# Revit family: НЕВАТОМ_Вентилятор ВР 86-77, Версия 2.с табл
name_source: partatom
category: Оборудование
revit_build: Autodesk Revit 2017 (Build: 20170118_1100(x64)
units: mm (PartAtom-declared; Revit-internal decimal feet)

## family parameters
Всегда вертикально = Да
На основе рабочей плоскости = Нет
Общий = Да
При загрузке вырезать с полостями = Нет
Размер круглого соединителя = Использовать диаметр
Тип детали = Нормальный
Точка расчета площади = Нет

## types (8) — shared parameters
(1.05Dн) = Нет
1.05Dн = Нет
ADSK_Количество = 1
ADSK_Количество фаз = 3
ADSK_Количество фаз числовое = 3
ADSK_Напряжение = 380 В
ADSK_Номинальная мощность = 0 Вт
ADSK_Ток = 0 А
l патрубка = 80 мм
Ключевая пометка = Вентиляция
ТП = НЕВАТОМ_Вентилятор ВР 86-77

## per-type parameters (varying)
- №2.5: (0.9Dн)=Да; (Dн)=Нет; 0.9Dн=Да; A1=162 мм; AA=175 мм; ADSK_Классификация нагрузок=ОВК; BB=175 мм; D=250 мм; D внешний=300 мм; D входного патрубка=250 мм; D/2=50 мм; D1=255 мм; Dн=Нет; H опоры=270 мм; H1=320 мм; L двиг=50 мм; L длина опоры=410 мм; R1=205 мм; R2=160 мм; Type=38 мм; a2=250 мм; b=20 мм; c1=205 мм; c2=205 мм; d двиг=100 мм; h=120 мм; h1=180 мм; h2=155 мм; h3=0 мм; k=30 мм; l двиг=120 мм; l длина=205 мм; r=50 мм; ВР=2.5 мм; Выбор исполнения=0 мм; Н2=572 мм; НЕВАТОМ_Исполнение вентилятора=2 мм; НЕВАТОМ_Мощность электродвигатель=0.18 мм; НЕВАТОМ_Частота вращения электродвигателя=1500; Ширина опоры=287 мм; Ширина основания=287 мм; типоразмер=2.5 мм
- №3.15: (0.9Dн)=Да; (Dн)=Нет; 0.9Dн=Да; A1=204 мм; AA=220 мм; BB=220 мм; D=315 мм; D внешний=365 мм; D входного патрубка=315 мм; D/2=50 мм; D1=320 мм; Dн=Нет; H опоры=346 мм; H1=396 мм; L двиг=50 мм; L длина опоры=467 мм; R1=257 мм; R2=200 мм; Type=39 мм; a2=315 мм; b=20 мм; c1=217 мм; c2=250 мм; d двиг=100 мм; h=120 мм; h1=220 мм; h2=200 мм; h3=100 мм; k=1 мм; l двиг=120 мм; l длина=250 мм; r=50 мм; ВР=3.15 мм; Выбор исполнения=1 мм; Н2=616 мм; НЕВАТОМ_Исполнение вентилятора=1 мм; НЕВАТОМ_Мощность электродвигатель=0.18 мм; НЕВАТОМ_Частота вращения электродвигателя=1500; Ширина опоры=287 мм; Ширина основания=287 мм; типоразмер=3.15 мм
- №4: (0.9Dн)=Нет; (Dн)=Да; 0.9Dн=Нет; A1=260 мм; AA=280 мм; BB=280 мм; D=400 мм; D внешний=450 мм; D входного патрубка=400 мм; D/2=50 мм; D1=405 мм; Dн=Да; H опоры=476 мм; H1=526 мм; L двиг=100 мм; L длина опоры=580 мм; R1=326 мм; R2=250 мм; Type=40 мм; a2=400 мм; b=25 мм; c1=290 мм; c2=290 мм; d двиг=100 мм; h=200 мм; h1=270 мм; h2=250 мм; h3=100 мм; k=1 мм; l двиг=80 мм; l длина=290 мм; r=50 мм; ВР=4 мм; Выбор исполнения=0 мм; Н2=796 мм; НЕВАТОМ_Исполнение вентилятора=1 мм; НЕВАТОМ_Мощность электродвигатель=0.75 мм; НЕВАТОМ_Частота вращения электродвигателя=1500; Ширина опоры=357 мм; Ширина основания=357 мм; типоразмер=4 мм
- №5: (0.9Dн)=Да; (Dн)=Нет; 0.9Dн=Да; A1=325 мм; AA=350 мм; BB=350 мм; D=500 мм; D внешний=550 мм; D входного патрубка=500 мм; D/2=50 мм; D1=505 мм; Dн=Нет; H опоры=600 мм; H1=650 мм; L двиг=100 мм; L длина опоры=754 мм; R1=400 мм; R2=310 мм; Type=39 мм; a2=500 мм; b=25 мм; c1=404 мм; c2=350 мм; d двиг=100 мм; h=150 мм; h1=335 мм; h2=310 мм; h3=100 мм; k=1 мм; l двиг=80 мм; l длина=350 мм; r=50 мм; ВР=5 мм; Выбор исполнения=0 мм; Н2=985 мм; НЕВАТОМ_Исполнение вентилятора=1 мм; НЕВАТОМ_Мощность электродвигатель=0.37 мм; НЕВАТОМ_Частота вращения электродвигателя=1000; Ширина опоры=476 мм; Ширина основания=476 мм; типоразмер=5 мм
- №6.3: (0.9Dн)=Да; (Dн)=Нет; 0.9Dн=Да; A1=409 мм; AA=441 мм; BB=441 мм; D=630 мм; D внешний=700 мм; D входного патрубка=630 мм; D/2=120 мм; D1=635 мм; Dн=Нет; H опоры=630 мм; H1=750 мм; L двиг=100 мм; L длина опоры=900 мм; R1=513 мм; R2=400 мм; Type=41 мм; a2=630 мм; b=25 мм; c1=550 мм; c2=350 мм; d двиг=240 мм; h=300 мм; h1=415 мм; h2=395 мм; h3=100 мм; k=1 мм; l двиг=300 мм; l длина=350 мм; r=120 мм; ВР=6.3 мм; Выбор исполнения=0 мм; Н2=1165 мм; НЕВАТОМ_Исполнение вентилятора=1 мм; НЕВАТОМ_Мощность электродвигатель=1.1 мм; НЕВАТОМ_Частота вращения электродвигателя=1000; Ширина опоры=556 мм; Ширина основания=556 мм; типоразмер=6.3 мм
- №8: (0.9Dн)=Да; (Dн)=Нет; 0.9Dн=Да; A1=520 мм; AA=560 мм; BB=560 мм; D=800 мм; D внешний=850 мм; D входного патрубка=800 мм; D/2=110 мм; D1=805 мм; Dн=Нет; H опоры=700 мм; H1=810 мм; L двиг=140 мм; L длина опоры=1074 мм; R1=650 мм; R2=500 мм; Type=41 мм; a2=800 мм; b=25 мм; c1=674 мм; c2=400 мм; d двиг=220 мм; h=300 мм; h1=540 мм; h2=500 мм; h3=100 мм; k=0 мм; l двиг=200 мм; l длина=400 мм; r=110 мм; ВР=8 мм; Выбор исполнения=0 мм; Н2=1350 мм; НЕВАТОМ_Исполнение вентилятора=1 мм; НЕВАТОМ_Мощность электродвигатель=1.5 мм; НЕВАТОМ_Частота вращения электродвигателя=1000; Ширина опоры=646 мм; Ширина основания=646 мм; типоразмер=8 мм
- №10: (0.9Dн)=Да; (Dн)=Нет; 0.9Dн=Да; A1=800 мм; AA=700 мм; BB=700 мм; D=1000 мм; D внешний=1050 мм; D входного патрубка=1000 мм; D/2=220 мм; D1=1005 мм; Dн=Нет; H опоры=1000 мм; H1=1220 мм; L двиг=200 мм; L длина опоры=1343 мм; R1=880 мм; R2=620 мм; Type=43 мм; a2=1150 мм; b=25 мм; c1=693 мм; c2=650 мм; d двиг=440 мм; h=300 мм; h1=660 мм; h2=620 мм; h3=100 мм; k=80 мм; l двиг=320 мм; l длина=650 мм; r=220 мм; ВР=10 мм; Выбор исполнения=0 мм; Н2=1880 мм; НЕВАТОМ_Исполнение вентилятора=1 мм; НЕВАТОМ_Мощность электродвигатель=11 мм; НЕВАТОМ_Частота вращения электродвигателя=750; Ширина опоры=480 мм; Ширина основания=930 мм; типоразмер=10 мм
- №12.5: (0.9Dн)=Да; (Dн)=Нет; 0.9Dн=Да; A1=900 мм; AA=875 мм; ADSK_Примечание=size_lookup(ТП, "", "нет типоразмера", D); BB=875 мм; D=1250 мм; D внешний=1300 мм; D входного патрубка=1250 мм; D/2=160 мм; D1=1255 мм; Dн=Нет; H опоры=1200 мм; H1=1360 мм; L двиг=340 мм; L длина опоры=1648 мм; R1=1050 мм; R2=780 мм; Type=43 мм; a2=1338 мм; b=25 мм; c1=848 мм; c2=800 мм; d двиг=320 мм; h=300 мм; h1=815 мм; h2=780 мм; h3=100 мм; k=80 мм; l двиг=500 мм; l длина=800 мм; r=160 мм; ВР=12.5 мм; Выбор исполнения=0 мм; Н2=2175 мм; НЕВАТОМ_Исполнение вентилятора=1 мм; НЕВАТОМ_Мощность электродвигатель=15 мм; НЕВАТОМ_Частота вращения электродвигателя=750; Ширина опоры=700 мм; Ширина основания=1520 мм; типоразмер=12.5 мм
